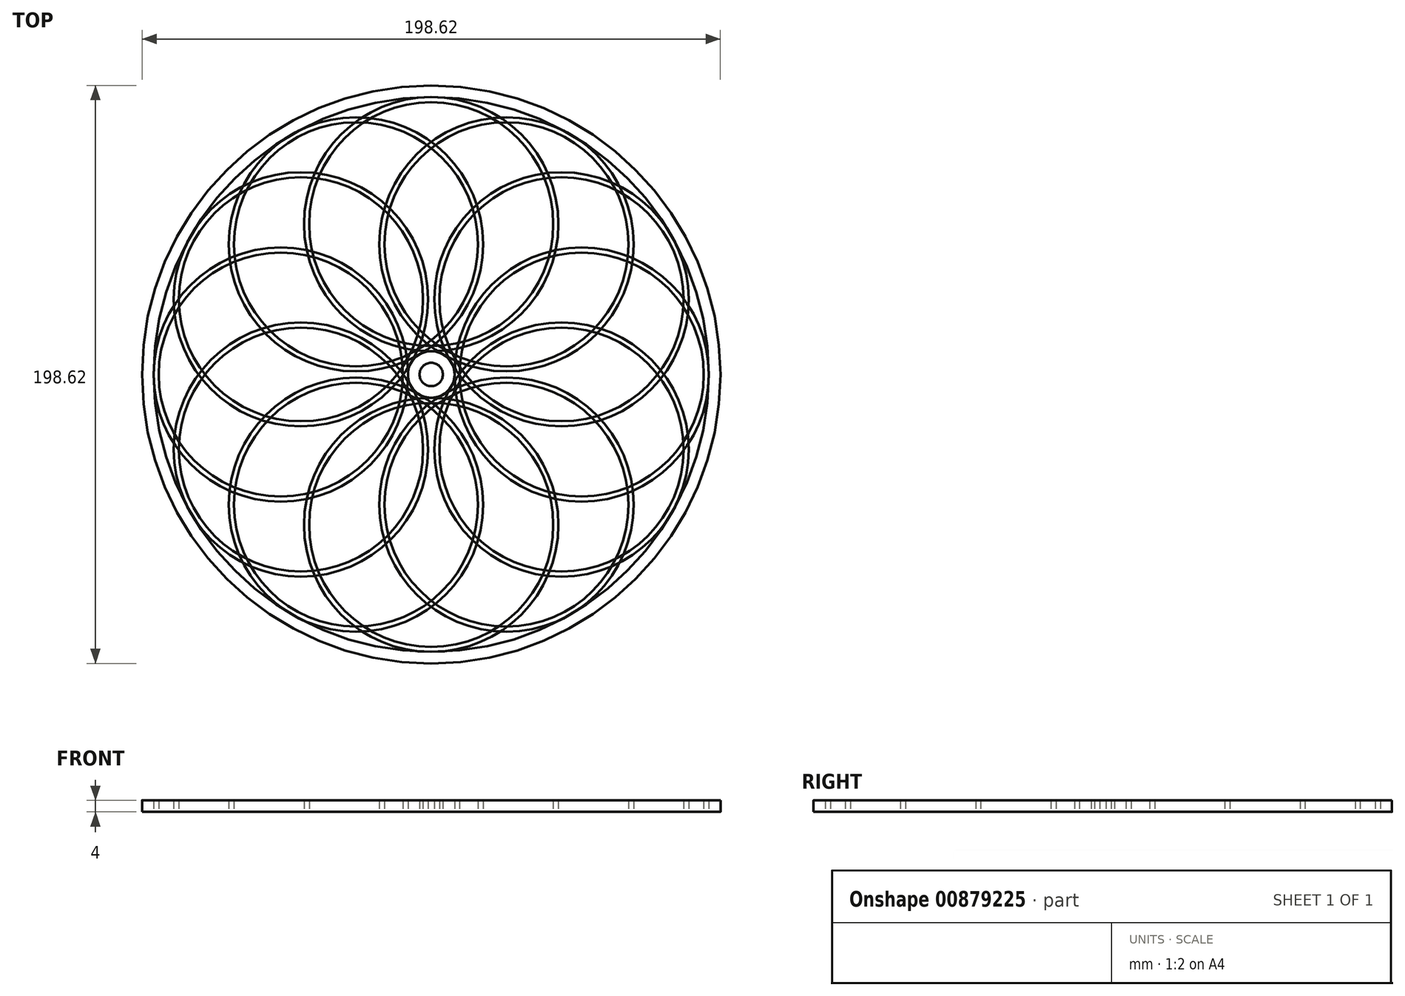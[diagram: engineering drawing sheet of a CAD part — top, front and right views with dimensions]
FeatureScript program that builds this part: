
annotation { "Feature Type Name" : "Feature", "Feature Type Description" : "" }
export const myFeature = defineFeature(function(context is Context, id is Id, definition is map)
    precondition{}
    {
        {
            assignVariable(context, id + "F0", {"name" : "GearWidth", "anyValue" : 4});
        }
        {
            assignVariable(context, id + "F1", {"name" : "InnerCircles", "anyValue" : 12});
        }
        {
            assignVariable(context, id + "F2", {"name" : "TeethNumber", "anyValue" : 120});
        }
        {
            var Q0;
            Q0=qCreatedBy(makeId("Top.planeOp"),FACE);
            var sketch = newSketch(context, id + "F3", { "sketchPlane" : qUnion([Q0])});
            skLineSegment(sketch, "E0", {"start": v(0, 127.06) * mm, "end": v(0, -95.31) * mm, "construction": true});
            skCircle(sketch, "E1", {"center": v(0, 0) * mm, "radius": 99.31 * mm});
            skCircle(sketch, "E2", {"center": v(0, 0) * mm, "radius": 95.31 * mm});
            skCircle(sketch, "E3", {"center": v(0, 0) * mm, "radius": 8 * mm});
            skCircle(sketch, "E4", {"center": v(0, 0) * mm, "radius": 4 * mm});
            skPoint(sketch, "E5", {"position": v(0, -8) * mm});
            skPoint(sketch, "E6", {"position": v(0, -51.66) * mm});
            skCircle(sketch, "E7", {"center": v(0, -51.66) * mm, "radius": 43.66 * mm});
            skCircle(sketch, "E8", {"center": v(0, -51.66) * mm, "radius": 41.9 * mm});
            skLineSegment(sketch, "E9", {"start": v(0, 0) * mm, "end": v(-10.94, 125.04) * mm, "construction": true});
            skCircle(sketch, "E10", {"center": v(0, 0) * mm, "radius": 110.3 * mm, "construction": true});
            skCircle(sketch, "E11", {"center": v(0, 0) * mm, "radius": 116.1 * mm, "construction": true});
            skSolve(sketch);
        }
        {
            var Q0;
            {var subQ0=sQuery(id+"F3.wireOp",EDGE,"1d8901da-11d4-4483-9926-b8bfcc8f3e3b");Q0=makeQuery(id+"F3.imprint","IMPRINT",FACE,{"disambiguationData":[TD([[makeQuery(id+"F3.imprint","IMPRINT",EDGE,{"derivedFrom":subQ0}),1.0]])]});}
            var Q1;
            Q1=makeQuery(id+"F3.imprint","IMPRINT",FACE,{"disambiguationData":[TD([[makeQuery(id+"F3.imprint","IMPRINT",EDGE,{"derivedFrom":sQuery(id+"F3.wireOp",EDGE,"E2")}),-1.0]])]});
            var Q2;
            Q2=makeQuery(id+"F3.imprint","IMPRINT",FACE,{"disambiguationData":[TD([[makeQuery(id+"F3.imprint","IMPRINT",EDGE,{"derivedFrom":sQuery(id+"F3.wireOp",EDGE,"E8")}),-1.0]])]});
            var Q3;
            Q3=makeQuery(id+"F3.imprint","IMPRINT",FACE,{"disambiguationData":[TD([[makeQuery(id+"F3.imprint","IMPRINT",EDGE,{"derivedFrom":sQuery(id+"F3.wireOp",EDGE,"E3")}),1.0]])]});
            extrude(context, id + "F4", {"entities" : qUnion([Q0, Q1, Q2, Q3]), "depth" : (getVariable(context, 'GearWidth')) * mm, "offsetDistance" : 25 * mm});
        }
        {
            var Q0;
            Q0=makeQuery(id+"F4.opExtrude","SWEPT_BODY",BODY,{"disambiguationData":[OSD([sQuery(id+"F3.wireOp",EDGE,"f96d612a-3d40-4833-af0c-4c8240c050c0"),sQuery(id+"F3.wireOp",EDGE,"26c351bc-3793-4e67-ba11-eadc3bd423690.MirrorCS"),sQuery(id+"F3.wireOp",EDGE,"E1"),sQuery(id+"F3.wireOp",EDGE,"E2")])]});
            var Q1;
            Q1=makeQuery(id+"F4.opExtrude","CAP_EDGE",EDGE,{"disambiguationData":[OSD([sQuery(id+"F3.wireOp",EDGE,"E4")])],"isStart":false});
            circularPattern(context, id + "F5", {"entities" : qUnion([Q0]), "axis" : qUnion([Q1]), "angle" : 360 * degree, "instanceCount" : getVariable(context, 'TeethNumber'), "equalSpace" : true});
        }
        {
            var Q0;
            Q0=makeQuery(id+"F4.opExtrude","SWEPT_BODY",BODY,{"disambiguationData":[OSD([sQuery(id+"F3.wireOp",EDGE,"E7"),sQuery(id+"F3.wireOp",EDGE,"E8")])]});
            var Q1;
            Q1=makeQuery(id+"F4.opExtrude","SWEPT_BODY",BODY,{"disambiguationData":[OSD([sQuery(id+"F3.wireOp",EDGE,"E3"),sQuery(id+"F3.wireOp",EDGE,"E4")])]});
            var Q2;
            Q2=sQuery(id+"F3.wireOp",EDGE,"E2");
            circularPattern(context, id + "F6", {"entities" : qUnion([Q0, Q1]), "axis" : qUnion([Q2]), "angle" : 360 * degree, "instanceCount" : getVariable(context, 'InnerCircles'), "equalSpace" : true});
        }
    });
